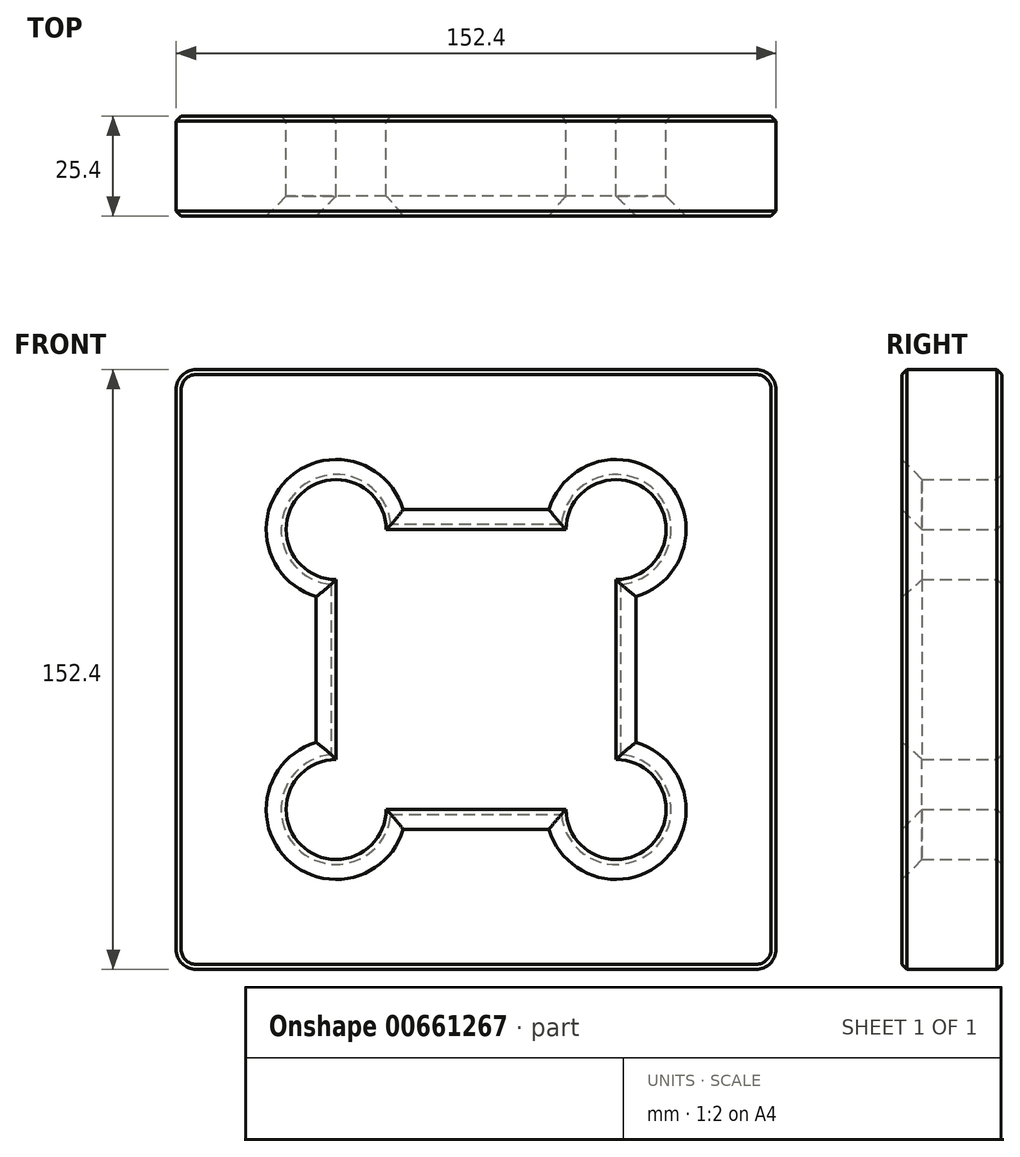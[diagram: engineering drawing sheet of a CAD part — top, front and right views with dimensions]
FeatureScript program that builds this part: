
annotation { "Feature Type Name" : "Feature", "Feature Type Description" : "" }
export const myFeature = defineFeature(function(context is Context, id is Id, definition is map)
    precondition{}
    {
        {
            var Q0;
            Q0=qCreatedBy(makeId("Front.planeOp"),FACE);
            var sketch = newSketch(context, id + "F0", { "sketchPlane" : qUnion([Q0])});
            skLineSegment(sketch, "E0.bottom", {"start": v(-71.94, 76.2) * mm, "end": v(80.46, 76.2) * mm});
            skLineSegment(sketch, "E0.top", {"start": v(-71.94, -76.2) * mm, "end": v(80.46, -76.2) * mm});
            skLineSegment(sketch, "E0.left", {"start": v(-71.94, 76.2) * mm, "end": v(-71.94, -76.2) * mm});
            skLineSegment(sketch, "E0.right", {"start": v(80.46, 76.2) * mm, "end": v(80.46, -76.2) * mm});
            skPoint(sketch, "E0.middle", {"position": v(4.26, 0) * mm});
            skLineSegment(sketch, "E1", {"start": v(-31.3, -76.2) * mm, "end": v(-31.3, 76.2) * mm});
            skLineSegment(sketch, "E2", {"start": v(39.82, 75.6) * mm, "end": v(39.82, -76.2) * mm});
            skLineSegment(sketch, "E3", {"start": v(-71.94, 35.56) * mm, "end": v(80.46, 35.56) * mm});
            skLineSegment(sketch, "E4", {"start": v(-71.94, -35.56) * mm, "end": v(80.46, -35.56) * mm});
            skCircle(sketch, "E5", {"center": v(-31.3, 35.56) * mm, "radius": 12.7 * mm});
            skCircle(sketch, "E6", {"center": v(-31.3, -35.56) * mm, "radius": 12.7 * mm});
            skCircle(sketch, "E7", {"center": v(39.82, -35.56) * mm, "radius": 12.7 * mm});
            skCircle(sketch, "E8", {"center": v(39.82, 35.56) * mm, "radius": 12.7 * mm});
            skSolve(sketch);
        }
        {
            var Q0;
            Q0 = qSketchRegion(id + "F0", true);
            extrude(context, id + "F1", {"entities" : qUnion([Q0]), "depth" : 25.4 * mm, "offsetDistance" : 25.4 * mm});
        }
        {
            var Q0;
            Q0=makeQuery(id+"F1.opExtrude","CAP_EDGE",EDGE,{"disambiguationData":[OSD([sQuery(id+"F0.wireOp",EDGE,"E2")])],"isStart":false});
            var Q1;
            Q1=makeQuery(id+"F1.opExtrude","CAP_EDGE",EDGE,{"disambiguationData":[OSD([sQuery(id+"F0.wireOp",EDGE,"E3")])],"isStart":false});
            var Q2;
            Q2=makeQuery(id+"F1.opExtrude","CAP_EDGE",EDGE,{"disambiguationData":[OSD([sQuery(id+"F0.wireOp",EDGE,"E4")])],"isStart":false});
            var Q3;
            Q3=makeQuery(id+"F1.opExtrude","CAP_EDGE",EDGE,{"disambiguationData":[OSD([sQuery(id+"F0.wireOp",EDGE,"E8")])],"isStart":false});
            var Q4;
            Q4=makeQuery(id+"F1.opExtrude","CAP_EDGE",EDGE,{"disambiguationData":[OSD([sQuery(id+"F0.wireOp",EDGE,"E7")])],"isStart":false});
            var Q5;
            Q5=makeQuery(id+"F1.opExtrude","CAP_EDGE",EDGE,{"disambiguationData":[OSD([sQuery(id+"F0.wireOp",EDGE,"E6")])],"isStart":false});
            var Q6;
            Q6=makeQuery(id+"F1.opExtrude","CAP_EDGE",EDGE,{"disambiguationData":[OSD([sQuery(id+"F0.wireOp",EDGE,"E1")])],"isStart":false});
            var Q7;
            Q7=makeQuery(id+"F1.opExtrude","CAP_EDGE",EDGE,{"disambiguationData":[OSD([sQuery(id+"F0.wireOp",EDGE,"E5")])],"isStart":false});
            chamfer(context, id + "F2", {"entities" : qUnion([Q0, Q1, Q2, Q3, Q4, Q5, Q6, Q7]), "width" : 5.08 * mm, "tangentPropagation" : true});
        }
        {
            var Q0;
            Q0=makeQuery(id+"F1.opExtrude","SWEPT_EDGE",EDGE,{"disambiguationData":[OSD([sQuery(id+"F0.wireOp",EDGE,"E0.bottom"),sQuery(id+"F0.wireOp",EDGE,"E0.right")])]});
            var Q1;
            Q1=makeQuery(id+"F1.opExtrude","SWEPT_EDGE",EDGE,{"disambiguationData":[OSD([sQuery(id+"F0.wireOp",EDGE,"E0.top"),sQuery(id+"F0.wireOp",EDGE,"E0.right")])]});
            var Q2;
            Q2=makeQuery(id+"F1.opExtrude","SWEPT_EDGE",EDGE,{"disambiguationData":[OSD([sQuery(id+"F0.wireOp",EDGE,"E0.top"),sQuery(id+"F0.wireOp",EDGE,"E0.left")])]});
            var Q3;
            Q3=makeQuery(id+"F1.opExtrude","SWEPT_EDGE",EDGE,{"disambiguationData":[OSD([sQuery(id+"F0.wireOp",EDGE,"E0.bottom"),sQuery(id+"F0.wireOp",EDGE,"E0.left")])]});
            fillet(context, id + "F3", {"entities" : qUnion([Q0, Q1, Q2, Q3]), "radius" : 5.08 * mm, "tangentPropagation" : true, "allowEdgeOverflow" : false});
        }
        {
            var Q0;
            Q0=makeQuery(id+"F1.opExtrude","CAP_EDGE",EDGE,{"disambiguationData":[OSD([sQuery(id+"F0.wireOp",EDGE,"E0.bottom")])],"isStart":false});
            var Q1;
            Q1=makeQuery(id+"F1.opExtrude","CAP_EDGE",EDGE,{"disambiguationData":[OSD([sQuery(id+"F0.wireOp",EDGE,"E0.left")])],"isStart":true});
            var Q2;
            Q2=makeQuery(id+"F1.opExtrude","CAP_EDGE",EDGE,{"disambiguationData":[OSD([sQuery(id+"F0.wireOp",EDGE,"E3")])],"isStart":true});
            var Q3;
            Q3=makeQuery(id+"F1.opExtrude","CAP_EDGE",EDGE,{"disambiguationData":[OSD([sQuery(id+"F0.wireOp",EDGE,"E5")])],"isStart":true});
            var Q4;
            Q4=makeQuery(id+"F1.opExtrude","CAP_EDGE",EDGE,{"disambiguationData":[OSD([sQuery(id+"F0.wireOp",EDGE,"E1")])],"isStart":true});
            var Q5;
            Q5=makeQuery(id+"F1.opExtrude","CAP_EDGE",EDGE,{"disambiguationData":[OSD([sQuery(id+"F0.wireOp",EDGE,"E2")])],"isStart":true});
            var Q6;
            Q6=makeQuery(id+"F1.opExtrude","CAP_EDGE",EDGE,{"disambiguationData":[OSD([sQuery(id+"F0.wireOp",EDGE,"E8")])],"isStart":true});
            var Q7;
            Q7=makeQuery(id+"F1.opExtrude","CAP_EDGE",EDGE,{"disambiguationData":[OSD([sQuery(id+"F0.wireOp",EDGE,"E4")])],"isStart":true});
            var Q8;
            Q8=makeQuery(id+"F1.opExtrude","CAP_EDGE",EDGE,{"disambiguationData":[OSD([sQuery(id+"F0.wireOp",EDGE,"E6")])],"isStart":true});
            var Q9;
            Q9=makeQuery(id+"F1.opExtrude","CAP_EDGE",EDGE,{"disambiguationData":[OSD([sQuery(id+"F0.wireOp",EDGE,"E7")])],"isStart":true});
            chamfer(context, id + "F4", {"entities" : qUnion([Q0, Q1, Q2, Q3, Q4, Q5, Q6, Q7, Q8, Q9]), "width" : 1.27 * mm, "tangentPropagation" : true});
        }
    });
